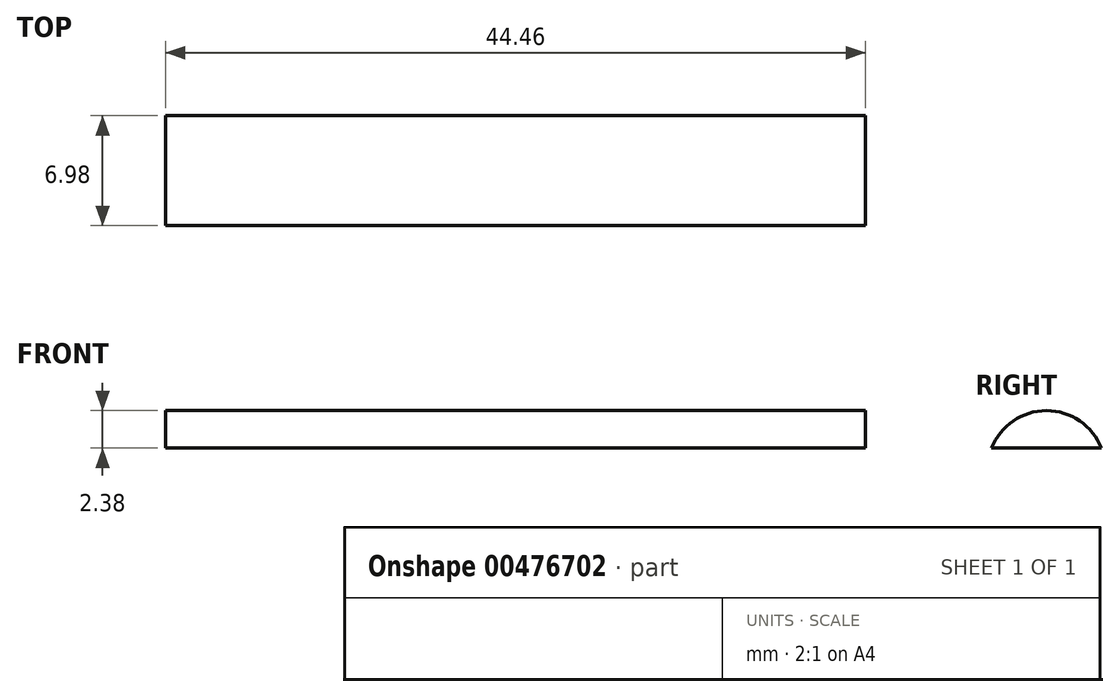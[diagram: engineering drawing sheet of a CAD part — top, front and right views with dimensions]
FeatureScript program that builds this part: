
annotation { "Feature Type Name" : "Feature", "Feature Type Description" : "" }
export const myFeature = defineFeature(function(context is Context, id is Id, definition is map)
    precondition{}
    {
        {
            var Q0;
            Q0=qCreatedBy(makeId("Top.planeOp"),FACE);
            var sketch = newSketch(context, id + "F0", { "sketchPlane" : qUnion([Q0])});
            skLineSegment(sketch, "E0.bottom", {"start": v(-22.23, 3.5) * mm, "end": v(22.23, 3.5) * mm});
            skLineSegment(sketch, "E0.top", {"start": v(-22.23, -3.5) * mm, "end": v(22.23, -3.5) * mm});
            skLineSegment(sketch, "E0.left", {"start": v(-22.23, 3.5) * mm, "end": v(-22.23, -3.5) * mm});
            skLineSegment(sketch, "E0.right", {"start": v(22.23, 3.5) * mm, "end": v(22.23, -3.5) * mm});
            skLineSegment(sketch, "E1", {"start": v(0, 3.5) * mm, "end": v(0, -3.5) * mm, "construction": true});
            skSolve(sketch);
        }
        {
            var Q0;
            Q0 = qSketchRegion(id + "F0", true);
            extrude(context, id + "F1", {"entities" : qUnion([Q0]), "depth" : 2.38 * mm});
        }
        {
            var Q0;
            Q0=makeQuery(id+"F1.opExtrude","SWEPT_FACE",FACE,{"disambiguationData":[OSD([sQuery(id+"F0.wireOp",EDGE,"E0.left")])]});
            var sketch = newSketch(context, id + "F2", { "sketchPlane" : qUnion([Q0])});
            skPoint(sketch, "E2", {"position": v(0, 2.38) * mm});
            skArc(sketch, "E3", {"start": v(3.5, 0) * mm, "mid": v(0, 2.38) * mm, "end": v(-3.5, 0) * mm});
            skLineSegment(sketch, "E4", {"start": v(-3.5, 0) * mm, "end": v(-3.5, 2.38) * mm});
            skLineSegment(sketch, "E5", {"start": v(-3.5, 2.38) * mm, "end": v(3.5, 2.38) * mm});
            skLineSegment(sketch, "E6", {"start": v(3.5, 2.38) * mm, "end": v(3.5, 0) * mm});
            skSolve(sketch);
        }
        {
            var Q0;
            Q0 = qSketchRegion(id + "F2", true);
            extrude(context, id + "F3", {"entities" : qUnion([Q0]), "operationType" : NewBodyOperationType.REMOVE, "endBound" : BoundingType.THROUGH_ALL, "oppositeDirection" : true, "depth" : 25.4 * mm});
        }
    });
